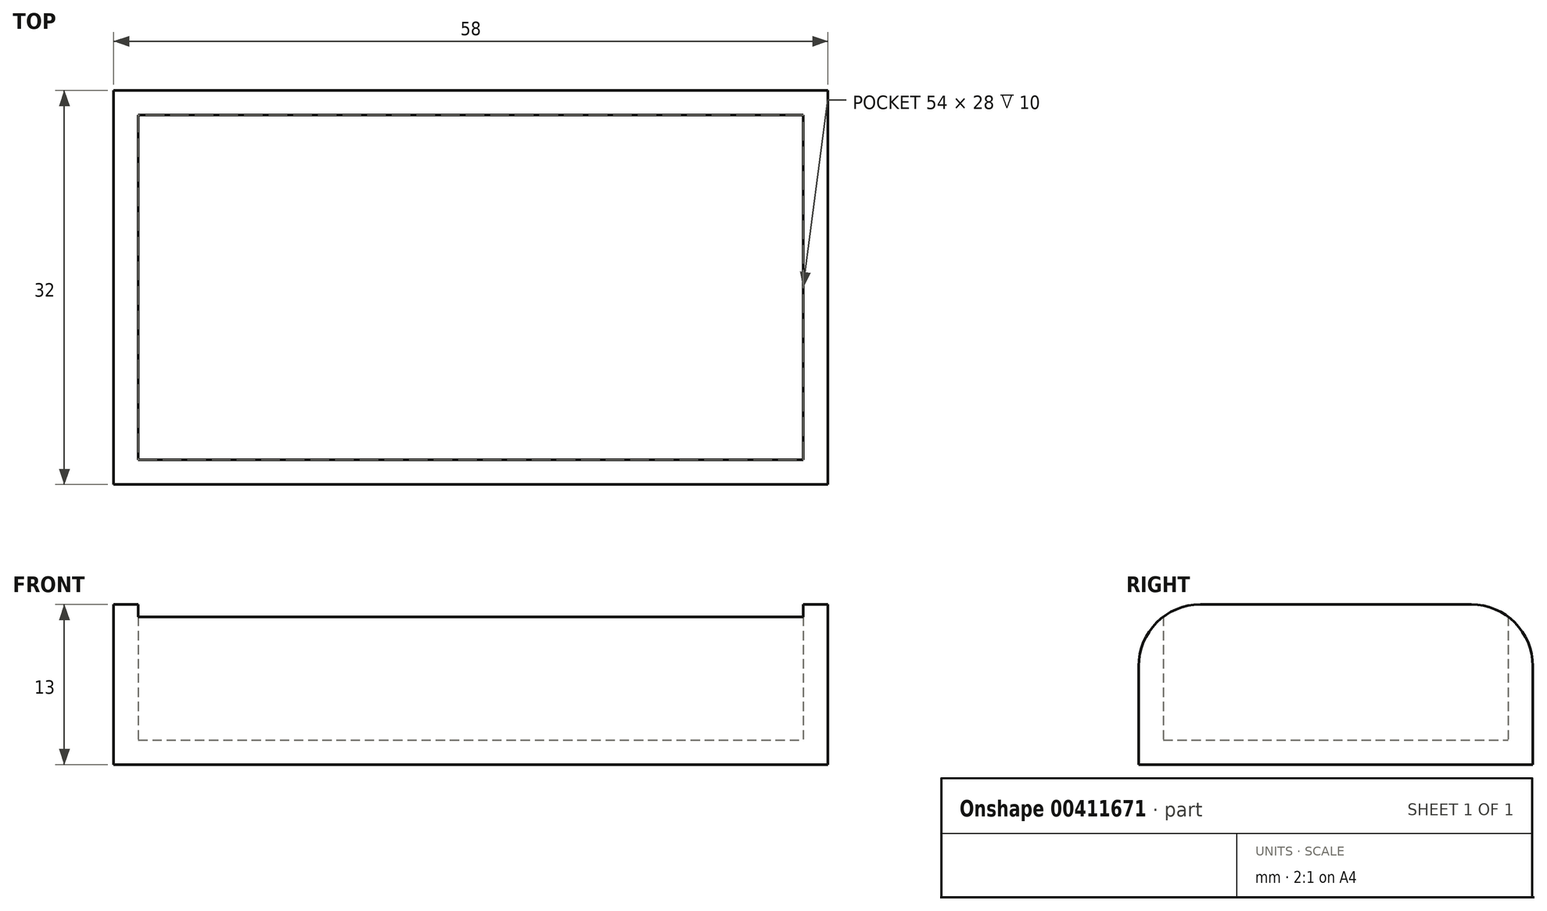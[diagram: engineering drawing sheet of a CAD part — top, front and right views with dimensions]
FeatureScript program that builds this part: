
annotation { "Feature Type Name" : "Feature", "Feature Type Description" : "" }
export const myFeature = defineFeature(function(context is Context, id is Id, definition is map)
    precondition{}
    {
        {
            var Q0;
            Q0=qCreatedBy(makeId("Top.planeOp"),FACE);
            var sketch = newSketch(context, id + "F0", { "sketchPlane" : qUnion([Q0])});
            skLineSegment(sketch, "E0.bottom", {"start": v(0, 0) * mm, "end": v(58, 0) * mm});
            skLineSegment(sketch, "E0.top", {"start": v(0, 32) * mm, "end": v(58, 32) * mm});
            skLineSegment(sketch, "E0.left", {"start": v(0, 0) * mm, "end": v(0, 32) * mm});
            skLineSegment(sketch, "E0.right", {"start": v(58, 0) * mm, "end": v(58, 32) * mm});
            skSolve(sketch);
        }
        {
            var Q0;
            Q0 = qSketchRegion(id + "F0", true);
            extrude(context, id + "F1", {"entities" : qUnion([Q0]), "depth" : 13 * mm});
        }
        {
            var Q0;
            Q0=makeQuery(id+"F1.opExtrude","CAP_FACE",FACE,{"disambiguationData":[OSD([sQuery(id+"F0.wireOp",EDGE,"E0.bottom"),sQuery(id+"F0.wireOp",EDGE,"E0.top"),sQuery(id+"F0.wireOp",EDGE,"E0.left"),sQuery(id+"F0.wireOp",EDGE,"E0.right")])],"isStart":false});
            shell(context, id + "F2", {"entities" : qUnion([Q0]), "thickness" : 2 * mm});
        }
        {
            var Q0;
            Q0=makeQuery(id+"F1.opExtrude","CAP_EDGE",EDGE,{"disambiguationData":[OSD([sQuery(id+"F0.wireOp",EDGE,"E0.bottom")])],"isStart":false});
            var Q1;
            Q1=makeQuery(id+"F1.opExtrude","CAP_EDGE",EDGE,{"disambiguationData":[OSD([sQuery(id+"F0.wireOp",EDGE,"E0.top")])],"isStart":false});
            fillet(context, id + "F3", {"entities" : qUnion([Q0, Q1]), "radius" : 5 * mm, "tangentPropagation" : true, "allowEdgeOverflow" : false});
        }
    });
